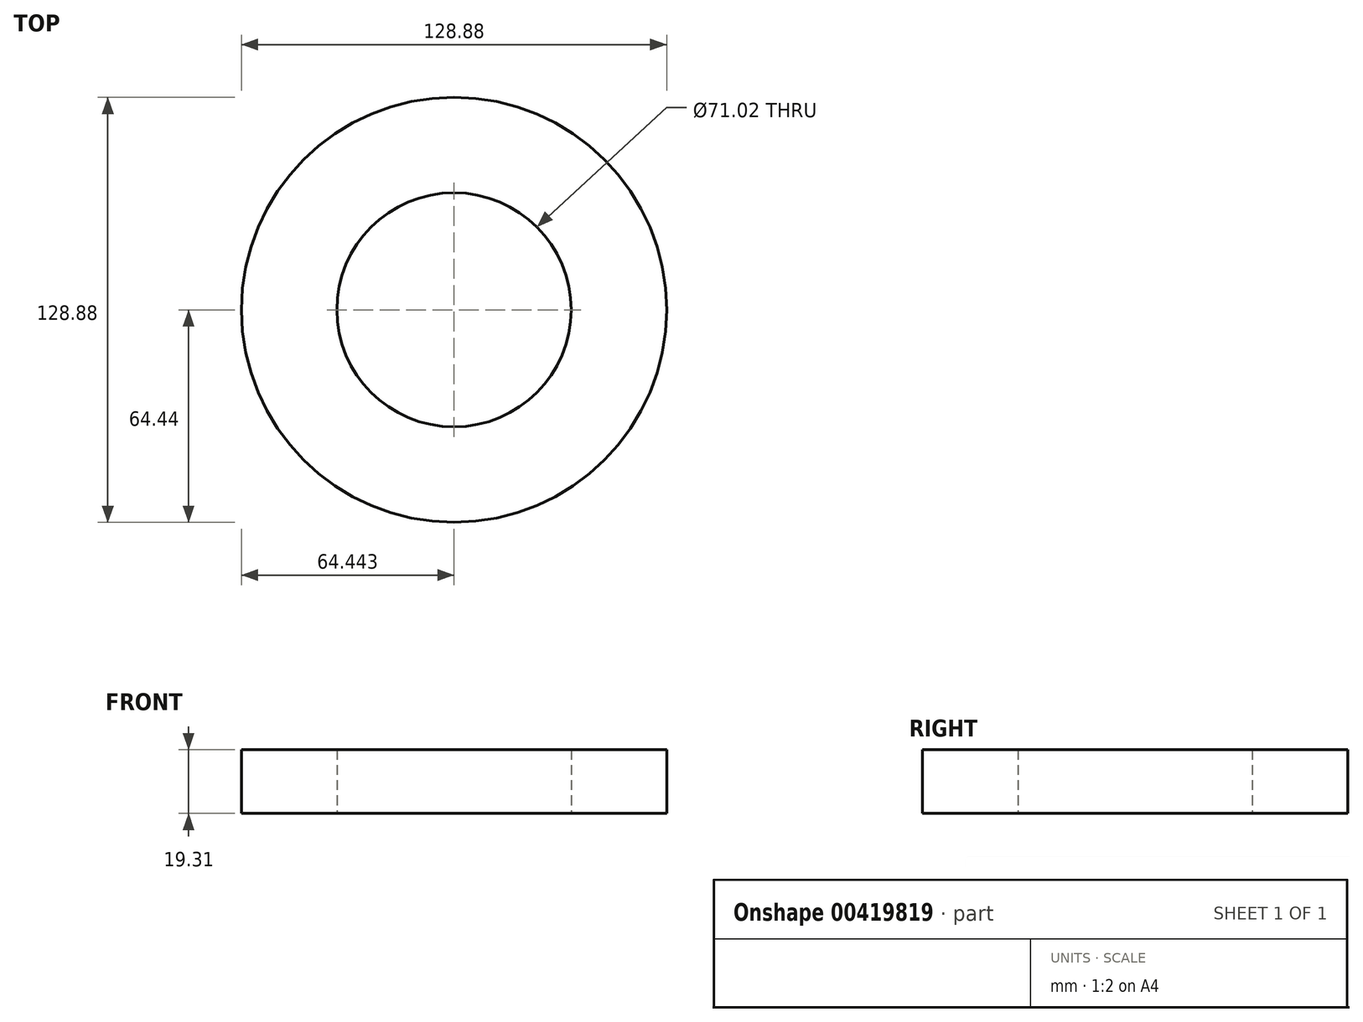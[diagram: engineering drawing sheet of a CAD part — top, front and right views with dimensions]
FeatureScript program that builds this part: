
annotation { "Feature Type Name" : "Feature", "Feature Type Description" : "" }
export const myFeature = defineFeature(function(context is Context, id is Id, definition is map)
    precondition{}
    {
        {
            var Q0;
            Q0=qCreatedBy(makeId("Top.planeOp"),FACE);
            var sketch = newSketch(context, id + "F0", { "sketchPlane" : qUnion([Q0])});
            skCircle(sketch, "E0", {"center": v(-347.12, 45.57) * mm, "radius": 35.5 * mm});
            skCircle(sketch, "E1", {"center": v(-347.12, 45.57) * mm, "radius": 64.44 * mm});
            skSolve(sketch);
        }
        {
            var Q0;
            Q0 = qSketchRegion(id + "F0", true);
            extrude(context, id + "F1", {"entities" : qUnion([Q0]), "depth" : 19.3 * mm});
        }
    });
